# Revit family: Mounted_Storage_&_Accessories-Teknion-RSEDS_Elevated_Desktop_Cabinet_Sliding_Doors-R2019
name_source: partatom
category: Furniture
units: mm (PartAtom-declared; Revit-internal decimal feet)

## family parameters
Always vertical = Yes
Cut with Voids When Loaded = No
OmniClass Number = 23.40.20.00
OmniClass Title = General Furniture and Specialties
Room Calculation Point = No
Shared = Yes
Work Plane-Based = No

## types (7) — shared parameters
Assembly Code = E2020200
Manufacturer = Teknion
Manufacturer Fax = 416.661.4586
Part Number = RSEDS
Product Documentation Link = https://www.teknion.com
Product Line = Expansion Desking
Product Page URL = https://www.teknion.com
Series = Expansion Desking
Sustainability Data = https://www.teknion.com
URL = www.teknion.com
Unit Weight URL = http://www.teknion.com
Warranty = http://www.teknion.com

## per-type parameters (varying)
| type | Accessory Finish | Accessory Finish Note | Description | Fabric | Laminate | Left Configuration | Model | Right Configuration | Shared Configuration | Whiteboard |
| Single-Sided, Laminate Accessory, 16" Depth | Source Laminate - Teknion - 3M - Provincial Oak | Select Source Laminate Material | Elevated Desktop Cabinet - Sliding Doors, Single - Sided Configuration, Laminate Accessory, 16" Depth | No | Yes | No | RSEDSSL_16__ | No | Yes | No |
| Left Configuration, Laminate Accessory, 16" Depth | Source Laminate - Teknion - 3M - Provincial Oak | Select Source Laminate Material | Elevated Desktop Cabinet - Sliding Doors, Left Configuration, Laminate Accessory, 16" Depth | No | Yes | Yes | RSEDSLL_16__ | No | No | No |
| Right Configuration, Laminate Accessory, 16" Depth | Source Laminate - Teknion - 3M - Provincial Oak | Select Source Laminate Material | Elevated Desktop Cabinet - Sliding Doors, Right Configuration, Laminate Accessory, 16" Depth | No | Yes | No | RSEDSRL_16__ | Yes | No | No |
| Left Configuration, Fabric Tackboard Accessory, 16" Depth | Fabric - Teknion - B142 - Digi Tweed - Rose Tweed | Select Fabric Material | Elevated Desktop Cabinet - Sliding Doors, Left Configuration, Fabric Tackboard Accessory, 16" Depth | Yes | No | Yes | RSEDSLF_16__ | No | No | No |
| Right Configuration, Fabric Tackboard, 16" Depth | Fabric - Teknion - B142 - Digi Tweed - Rose Tweed | Select Fabric Material | Elevated Desktop Cabinet - Sliding Doors, Right Configuration, Fabric Tackboard Accessory, 16" Depth | Yes | No | No | RSEDSRF_16__ | Yes | No | No |
| Right Configuration, Whiteboard Accessory, 16" Depth | Metal-Teknion-WZ-Whiteboard | Select Whiteboard Material | Elevated Desktop Cabinet - Sliding Doors, Right Configuration, Whiteboard Accessory, 16" Depth | No | No | No | RSEDSRW_16__ | Yes | No | Yes |
| Left Configuration, Whiteboard Accessory, 16" Depth | Metal-Teknion-WZ-Whiteboard | Select Whiteboard Material | Elevated Desktop Cabinet - Sliding Doors, Left Configuration, Whiteboard Accessory, 16" Depth | No | No | Yes | RSEDSLW_16__ | No | No | Yes |

## geometry (parser evidence)
native form markers: Sweep x3
no freeform markers — native parametric forms only
